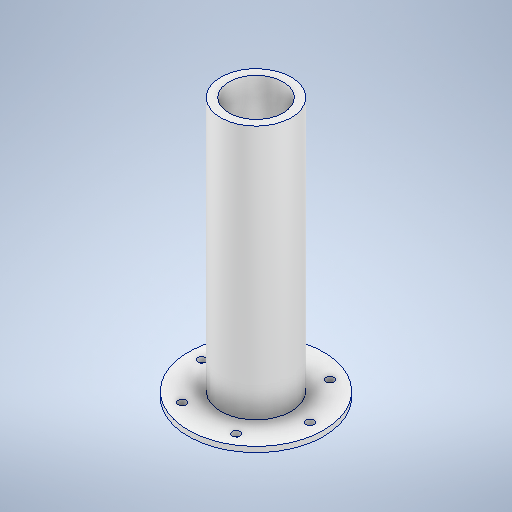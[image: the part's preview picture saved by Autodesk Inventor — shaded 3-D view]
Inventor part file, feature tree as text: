
AUTODESK INVENTOR PART (.ipt)
format: ipt  version: 2025.2 (Build 292293000, 293)  size: 292,864 bytes
history: native  units: mm
features: sketch x6, extrude x5, thread x1
ambient origin geometry x8: Origin, YZ Plane, XZ Plane, XY Plane, X Axis, Y Axis, Z Axis, Center Point
bodies: Solid1 (feature_tree)
feature tree (12):
  extrude  "Extrusion1"  Depth=5.5mm TaperAngle=0.0deg
  extrude  "Extrusion2"  Depth=2.0mm TaperAngle=0.0deg
  extrude  "Extrusion3"  Depth=94.0mm TaperAngle=0.0deg
  extrude  "Extrusion4"  TaperAngle=0.0deg  [1 undecoded]
  thread  "Thread2"  [1 undecoded]
  extrude  "Extrusion5"  Depth=3.0mm
  sketch  "Sketch1"  dims[d0=6.0mm d1=5.5mm d2=0.0mm]
  sketch  "Sketch2"  dims[d6=20.0mm d7=94.0mm d8=0.0mm]
  sketch  "Sketch3"  dims[d9=2.0mm d10=0.0mm d11=0.0mm d14=5.5mm d15=0.0mm]
  sketch  "Sketch4"  dims[d16=40.0mm d17=3.0mm]
  sketch  "Sketch5"  dims[d18=60.0mm d20=360.0deg d22=0.0mm d23=0.0mm d24=26.0mm]
  sketch  "Sketch Circular Pattern1"  dims[d3=50.0mm d4=2.0mm d5=0.0mm]
note: 2 required parameter values undecoded (feature->parameter linkage not recoverable at this tier; creation-order binding heuristic only, values carry confidence <= 0.55)
